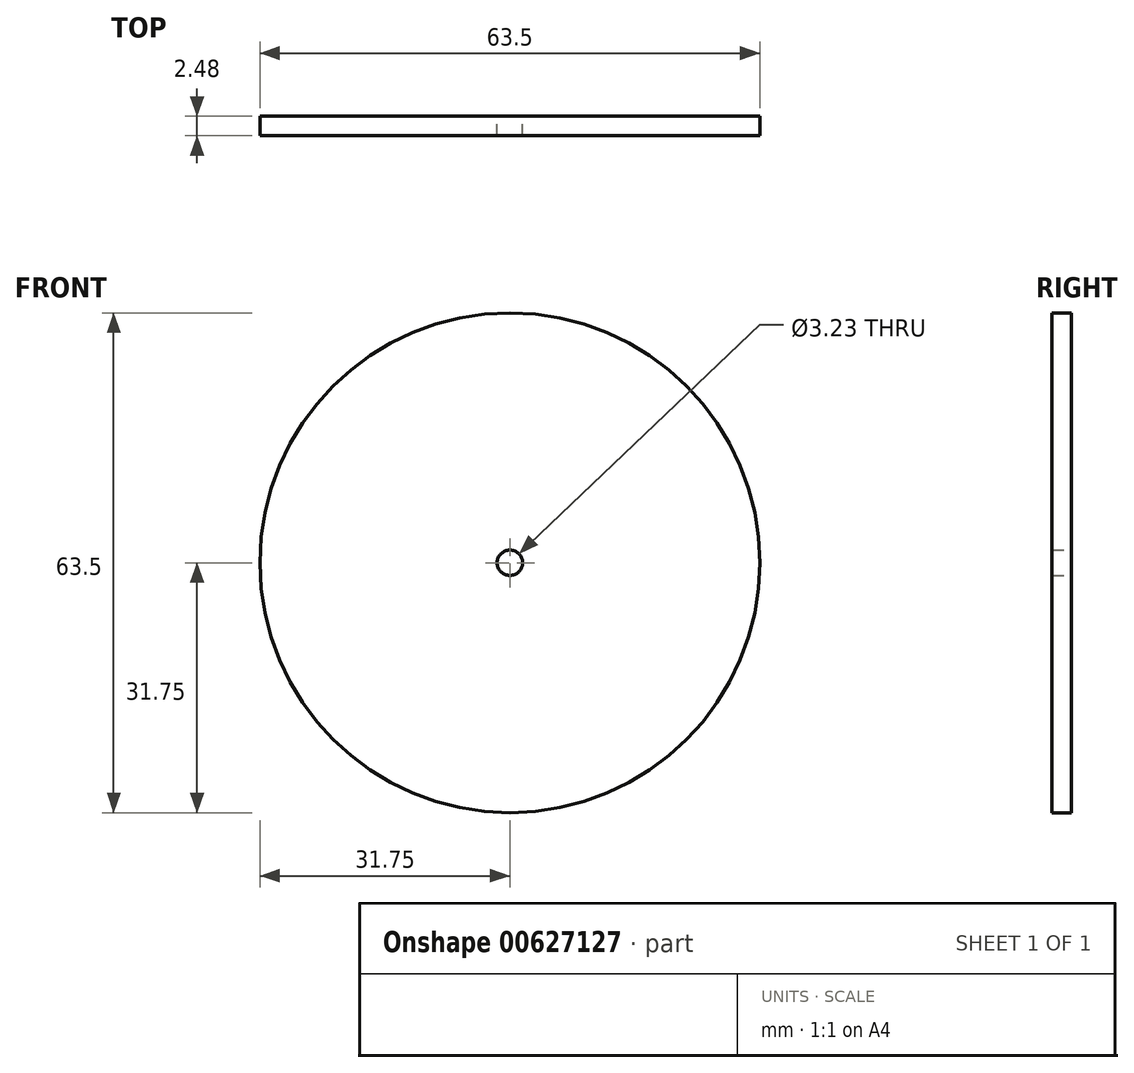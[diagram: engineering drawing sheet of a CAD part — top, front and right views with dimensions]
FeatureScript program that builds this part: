
annotation { "Feature Type Name" : "Feature", "Feature Type Description" : "" }
export const myFeature = defineFeature(function(context is Context, id is Id, definition is map)
    precondition{}
    {
        {
            var Q0;
            Q0=qCreatedBy(makeId("Front.planeOp"),FACE);
            var sketch = newSketch(context, id + "F0", { "sketchPlane" : qUnion([Q0])});
            skCircle(sketch, "E0", {"center": v(0, 0) * mm, "radius": 31.75 * mm});
            skCircle(sketch, "E1", {"center": v(0, 0) * mm, "radius": 1.61 * mm});
            skSolve(sketch);
        }
        {
            var Q0;
            Q0=makeQuery(id+"F0.imprint","IMPRINT",FACE,{"disambiguationData":[TD([[makeQuery(id+"F0.imprint","IMPRINT",EDGE,{"derivedFrom":sQuery(id+"F0.wireOp",EDGE,"E0")}),1.0]])]});
            extrude(context, id + "F1", {"entities" : qUnion([Q0]), "endBound" : BoundingType.SYMMETRIC, "depth" : 2.5 * mm, "offsetDistance" : 25.4 * mm});
        }
    });
